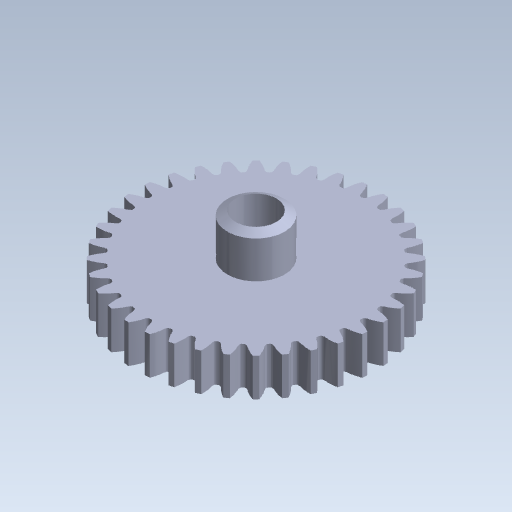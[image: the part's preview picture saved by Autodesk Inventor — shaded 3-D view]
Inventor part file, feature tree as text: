
AUTODESK INVENTOR PART (.ipt)
format: ipt  version: 2020 (Build 240168000, 168)  size: 327,680 bytes
history: native  units: mm (DEFAULTED — no unit token found)
features: chamfer x1
ambient origin geometry x8: Origin, YZ Plane, XZ Plane, XY Plane, X Axis, Y Axis, Z Axis, Center Point
bodies: Solid1 (feature_tree)
feature tree (1):
  chamfer  "Chamfer1"  [1 undecoded]
note: 1 required parameter value undecoded (feature->parameter linkage not recoverable at this tier; creation-order binding heuristic only, values carry confidence <= 0.55)
